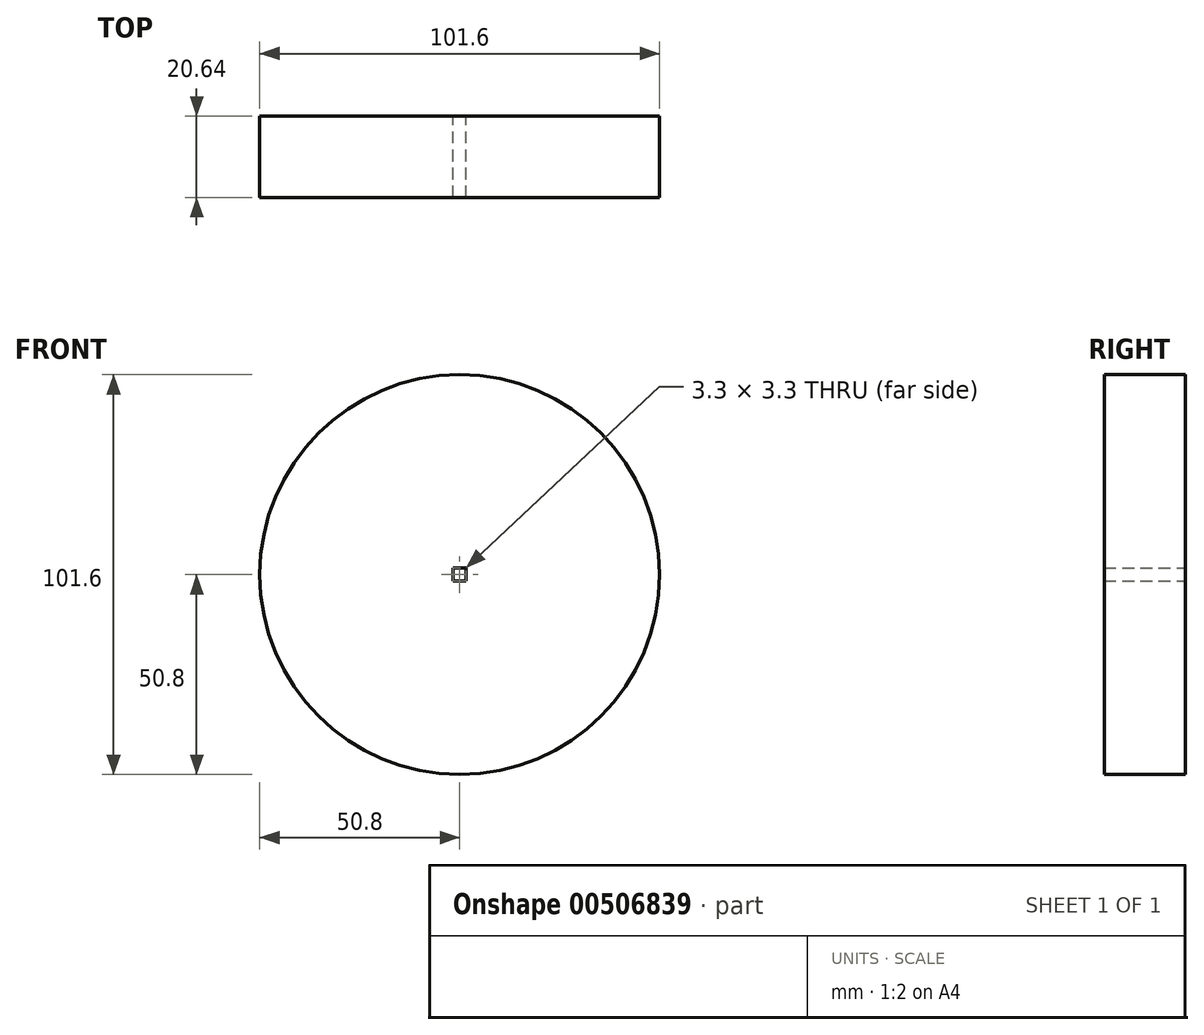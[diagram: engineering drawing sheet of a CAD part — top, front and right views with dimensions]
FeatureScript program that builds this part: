
annotation { "Feature Type Name" : "Feature", "Feature Type Description" : "" }
export const myFeature = defineFeature(function(context is Context, id is Id, definition is map)
    precondition{}
    {
        {
            var Q0;
            Q0=qCreatedBy(makeId("Front.planeOp"),FACE);
            var sketch = newSketch(context, id + "F0", { "sketchPlane" : qUnion([Q0])});
            skCircle(sketch, "E0", {"center": v(0, 0) * mm, "radius": 50.8 * mm});
            skLineSegment(sketch, "E1.bottom", {"start": v(1.65, 1.65) * mm, "end": v(-1.65, 1.65) * mm});
            skLineSegment(sketch, "E1.top", {"start": v(1.65, -1.65) * mm, "end": v(-1.65, -1.65) * mm});
            skLineSegment(sketch, "E1.left", {"start": v(1.65, 1.65) * mm, "end": v(1.65, -1.65) * mm});
            skLineSegment(sketch, "E1.right", {"start": v(-1.65, 1.65) * mm, "end": v(-1.65, -1.65) * mm});
            skSolve(sketch);
        }
        {
            var Q0;
            Q0=makeQuery(id+"F0.imprint","IMPRINT",FACE,{"disambiguationData":[TD([[makeQuery(id+"F0.imprint","IMPRINT",EDGE,{"derivedFrom":sQuery(id+"F0.wireOp",EDGE,"E0")}),1.0]])]});
            extrude(context, id + "F1", {"entities" : qUnion([Q0]), "depth" : 20.64 * mm, "offsetDistance" : 25.4 * mm});
        }
    });
